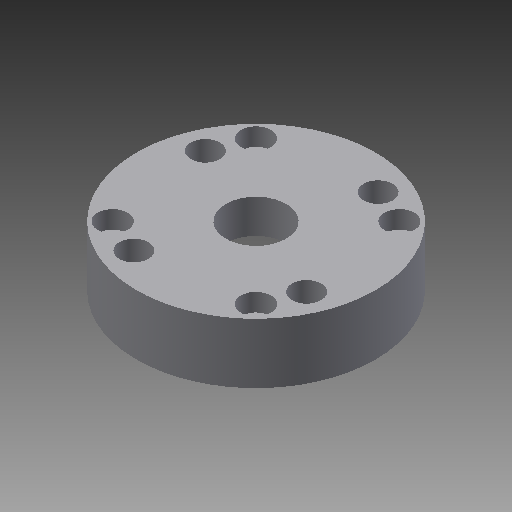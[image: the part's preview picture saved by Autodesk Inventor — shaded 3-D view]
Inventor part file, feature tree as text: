
AUTODESK INVENTOR PART (.ipt)
format: ipt  version: 2019.4 (Build 234330000, 330)  size: 296,448 bytes
history: native  units: in
note: dims shown in document units (in); Inventor stores cm internally (conversion verified against a paired STEP export)
features: other x322, sketch x10, hole x6, revolve x4, thread x1, pattern_linear x1
ambient origin geometry x8: Origin, YZ Plane, XZ Plane, XY Plane, X Axis, Y Axis, Z Axis, Center Point
bodies: Solid1 (feature_tree)
feature tree (344):
  revolve  "Revolution1"  Angle=360.0deg
  revolve  "Revolution2"  Angle=360.0deg
  thread  "Thread1"  [1 undecoded]
  revolve  "Revolution3"  [1 undecoded]
  hole  "Hole1"  [1 undecoded]
  hole  "Hole2"  [1 undecoded]
  hole  "Hole3"  [1 undecoded]
  hole  "Hole4"  [1 undecoded]
  hole  "Hole5"  [1 undecoded]
  revolve  "Revolution4"  [1 undecoded]
  hole  "Hole6"  [1 undecoded]
  pattern_linear  "Rectangular Pattern1"  [2 undecoded]
  other  "a1_XY"
  other  "a1_YZ"
  other  "a1_ZX"
  other  "a1_X"
  other  "a1_Y"
  other  "a1_Z"
  other  "a1_Center"
  other  "a2_XY"
  other  "a2_YZ"
  other  "a2_ZX"
  other  "a2_X"
  other  "a2_Y"
  other  "a2_Z"
  other  "a2_Center"
  other  "ab_tr1_XY"
  other  "ab_tr1_YZ"
  other  "ab_tr1_ZX"
  other  "ab_tr1_X"
  other  "ab_tr1_Y"
  other  "ab_tr1_Z"
  other  "ab_tr1_Center"
  other  "ab_tr2_XY"
  other  "ab_tr2_YZ"
  other  "ab_tr2_ZX"
  other  "ab_tr2_X"
  other  "ab_tr2_Y"
  other  "ab_tr2_Z"
  other  "ab_tr2_Center"
  other  "ab_tr3_XY"
  other  "ab_tr3_YZ"
  other  "ab_tr3_ZX"
  other  "ab_tr3_X"
  other  "ab_tr3_Y"
  other  "ab_tr3_Z"
  other  "ab_tr3_Center"
  other  "ab_tr4_XY"
  other  "ab_tr4_YZ"
  other  "ab_tr4_ZX"
  other  "ab_tr4_X"
  other  "ab_tr4_Y"
  other  "ab_tr4_Z"
  other  "ab_tr4_Center"
  other  "ar3_XY"
  other  "ar3_YZ"
  other  "ar3_ZX"
  other  "ar3_X"
  other  "ar3_Y"
  other  "ar3_Z"
  other  "ar3_Center"
  other  "ar4_XY"
  other  "ar4_YZ"
  other  "ar4_ZX"
  other  "ar4_X"
  other  "ar4_Y"
  other  "ar4_Z"
  other  "ar4_Center"
  other  "ar5_XY"
  other  "ar5_YZ"
  other  "ar5_ZX"
  other  "ar5_X"
  other  "ar5_Y"
  other  "ar5_Z"
  other  "ar5_Center"
  other  "ar6_XY"
  other  "ar6_YZ"
  other  "ar6_ZX"
  other  "ar6_X"
  other  "ar6_Y"
  other  "ar6_Z"
  other  "ar6_Center"
  other  "b1_XY"
  other  "b1_YZ"
  other  "b1_ZX"
  other  "b1_X"
  other  "b1_Y"
  other  "b1_Z"
  other  "b1_Center"
  other  "c11_XY"
  other  "c11_YZ"
  other  "c11_ZX"
  other  "c11_X"
  other  "c11_Y"
  other  "c11_Z"
  other  "c11_Center"
  other  "c22_XY"
  other  "c22_YZ"
  other  "c22_ZX"
  other  "c22_X"
  other  "c22_Y"
  other  "c22_Z"
  other  "c22_Center"
  other  "d11_XY"
  other  "d11_YZ"
  other  "d11_ZX"
  other  "d11_X"
  other  "d11_Y"
  other  "d11_Z"
  other  "d11_Center"
  other  "d22_XY"
  other  "d22_YZ"
  other  "d22_ZX"
  other  "d22_X"
  other  "d22_Y"
  other  "d22_Z"
  other  "d22_Center"
  other  "j_XY"
  other  "j_YZ"
  other  "j_ZX"
  other  "j_X"
  other  "j_Y"
  other  "j_Z"
  other  "j_Center"
  other  "k1_XY"
  other  "k1_YZ"
  other  "k1_ZX"
  other  "k1_X"
  other  "k1_Y"
  other  "k1_Z"
  other  "k1_Center"
  other  "k2_XY"
  other  "k2_YZ"
  other  "k2_ZX"
  other  "k2_X"
  other  "k2_Y"
  other  "k2_Z"
  other  "k2_Center"
  other  "nut_XY"
  other  "nut_YZ"
  other  "nut_ZX"
  other  "nut_X"
  other  "nut_Y"
  other  "nut_Z"
  other  "nut_Center"
  other  "po1_XY"
  other  "po1_YZ"
  other  "po1_ZX"
  other  "po1_X"
  other  "po1_Y"
  other  "po1_Z"
  other  "po1_Center"
  other  "po2_XY"
  other  "po2_YZ"
  other  "po2_ZX"
  other  "po2_X"
  other  "po2_Y"
  other  "po2_Z"
  other  "po2_Center"
  other  "po3_XY"
  other  "po3_YZ"
  other  "po3_ZX"
  other  "po3_X"
  other  "po3_Y"
  other  "po3_Z"
  other  "po3_Center"
  other  "po4_XY"
  other  "po4_YZ"
  other  "po4_ZX"
  other  "po4_X"
  other  "po4_Y"
  other  "po4_Z"
  other  "po4_Center"
  other  "r7_XY"
  other  "r7_YZ"
  other  "r7_ZX"
  other  "r7_X"
  other  "r7_Y"
  other  "r7_Z"
  other  "r7_Center"
  other  "r71_XY"
  other  "r71_YZ"
  other  "r71_ZX"
  other  "r71_X"
  other  "r71_Y"
  other  "r71_Z"
  other  "r71_Center"
  other  "r72_XY"
  other  "r72_YZ"
  other  "r72_ZX"
  other  "r72_X"
  other  "r72_Y"
  other  "r72_Z"
  other  "r72_Center"
  other  "r73_XY"
  other  "r73_YZ"
  other  "r73_ZX"
  other  "r73_X"
  other  "r73_Y"
  other  "r73_Z"
  other  "r73_Center"
  other  "rg_XY"
  other  "rg_YZ"
  other  "rg_ZX"
  other  "rg_X"
  other  "rg_Y"
  other  "rg_Z"
  other  "rg_Center"
  other  "rh_XY"
  other  "rh_YZ"
  other  "rh_ZX"
  other  "rh_X"
  other  "rh_Y"
  other  "rh_Z"
  other  "rh_Center"
  other  "rs_1_XY"
  other  "rs_1_YZ"
  other  "rs_1_ZX"
  other  "rs_1_X"
  other  "rs_1_Y"
  other  "rs_1_Z"
  other  "rs_1_Center"
  other  "rs_2_XY"
  other  "rs_2_YZ"
  other  "rs_2_ZX"
  other  "rs_2_X"
  other  "rs_2_Y"
  other  "rs_2_Z"
  other  "rs_2_Center"
  other  "rs_3_XY"
  other  "rs_3_YZ"
  other  "rs_3_ZX"
  other  "rs_3_X"
  other  "rs_3_Y"
  other  "rs_3_Z"
  other  "rs_3_Center"
  other  "rs_4_XY"
  other  "rs_4_YZ"
  other  "rs_4_ZX"
  other  "rs_4_X"
  other  "rs_4_Y"
  other  "rs_4_Z"
  other  "rs_4_Center"
  other  "sc1_XY"
  other  "sc1_YZ"
  other  "sc1_ZX"
  other  "sc1_X"
  other  "sc1_Y"
  other  "sc1_Z"
  other  "sc1_Center"
  other  "sc2_XY"
  other  "sc2_YZ"
  other  "sc2_ZX"
  other  "sc2_X"
  other  "sc2_Y"
  other  "sc2_Z"
  other  "sc2_Center"
  other  "sc3_XY"
  other  "sc3_YZ"
  other  "sc3_ZX"
  other  "sc3_X"
  other  "sc3_Y"
  other  "sc3_Z"
  other  "sc3_Center"
  other  "sc4_XY"
  other  "sc4_YZ"
  other  "sc4_ZX"
  other  "sc4_X"
  other  "sc4_Y"
  other  "sc4_Z"
  other  "sc4_Center"
  other  "to_dummy_XY"
  other  "to_dummy_YZ"
  other  "to_dummy_ZX"
  other  "to_dummy_X"
  other  "to_dummy_Y"
  other  "to_dummy_Z"
  other  "to_dummy_Center"
  other  "to_nut_XY"
  other  "to_nut_YZ"
  other  "to_nut_ZX"
  other  "to_nut_X"
  other  "to_nut_Y"
  other  "to_nut_Z"
  other  "to_nut_Center"
  other  "to_rod_XY"
  other  "to_rod_YZ"
  other  "to_rod_ZX"
  other  "to_rod_X"
  other  "to_rod_Y"
  other  "to_rod_Z"
  other  "to_rod_Center"
  other  "to_tube_XY"
  other  "to_tube_YZ"
  other  "to_tube_ZX"
  other  "to_tube_X"
  other  "to_tube_Y"
  other  "to_tube_Z"
  other  "to_tube_Center"
  other  "to_wiper_XY"
  other  "to_wiper_YZ"
  other  "to_wiper_ZX"
  other  "to_wiper_X"
  other  "to_wiper_Y"
  other  "to_wiper_Z"
  other  "to_wiper_Center"
  other  "track1_XY"
  other  "track1_YZ"
  other  "track1_ZX"
  other  "track1_X"
  other  "track1_Y"
  other  "track1_Z"
  other  "track1_Center"
  other  "track2_XY"
  other  "track2_YZ"
  other  "track2_ZX"
  other  "track2_X"
  other  "track2_Y"
  other  "track2_Z"
  other  "track2_Center"
  other  "track3_XY"
  other  "track3_YZ"
  other  "track3_ZX"
  other  "track3_X"
  other  "track3_Y"
  other  "track3_Z"
  other  "track3_Center"
  other  "track4_XY"
  other  "track4_YZ"
  other  "track4_ZX"
  other  "track4_X"
  other  "track4_Y"
  other  "track4_Z"
  other  "track4_Center"
  sketch  "Sketch_1"  dims[d0=360.0deg d1=360.0deg]
  sketch  "Sketch_84"  dims[d54=0.0in d55=0.0in d56=0.0in d57=0.0in d58=0.0in d59=0.0in d60=0.0in d61=0.0in d62=0.0in d63=0.0in d64=0.0in d65=0.0in d66=0.0in d67=0.0in d68=0.0in d69=0.0in d70=0.0in d71=0.0in d72=0.0in d73=0.0in d74=0.0in d75=0.0in d76=0.0in d77=0.0in d78=0.0in d79=0.0in d80=0.0in d81=0.0in d82=0.0in d83=0.0in d84=0.0in d85=0.0in d86=0.0in d87=0.0in]
  sketch  "Sketch_85"
  sketch  "Sketch4"  dims[d2=0.3302in d3=0.0in d4=360.0deg]
  sketch  "Sketch5"  dims[d5=0.156in d6=0.75in d7=0.25in d8=0.148in d9=0.5635in d10=0.5in d11=0.0in]
  sketch  "Sketch6"  dims[d12=0.156in d13=0.75in d14=0.25in d15=0.148in d16=0.5635in d17=0.5in d18=0.0in]
  sketch  "Sketch7"  dims[d19=0.156in d20=0.75in d21=0.25in d22=0.148in d23=0.5635in d24=0.5in d25=0.0in]
  sketch  "Sketch8"  dims[d26=0.156in d27=0.75in d28=0.25in d29=0.148in d30=0.5635in d31=0.5in d32=0.0in]
  sketch  "Sketch_9"  dims[d33=0.502in d34=0.75in d35=0.375in d36=0.25in d37=0.5635in d38=0.5in d39=0.0in d40=360.0deg]
  sketch  "Sketch10"  dims[d41=0.154in d42=0.75in d43=0.242in d44=0.18in d45=0.5635in d46=0.5in d47=0.0in d48=0.7874in d50=1.1003in d51=0.7874in d53=1.1003in]
note: 11 required parameter values undecoded (feature->parameter linkage not recoverable at this tier; creation-order binding heuristic only, values carry confidence <= 0.55)